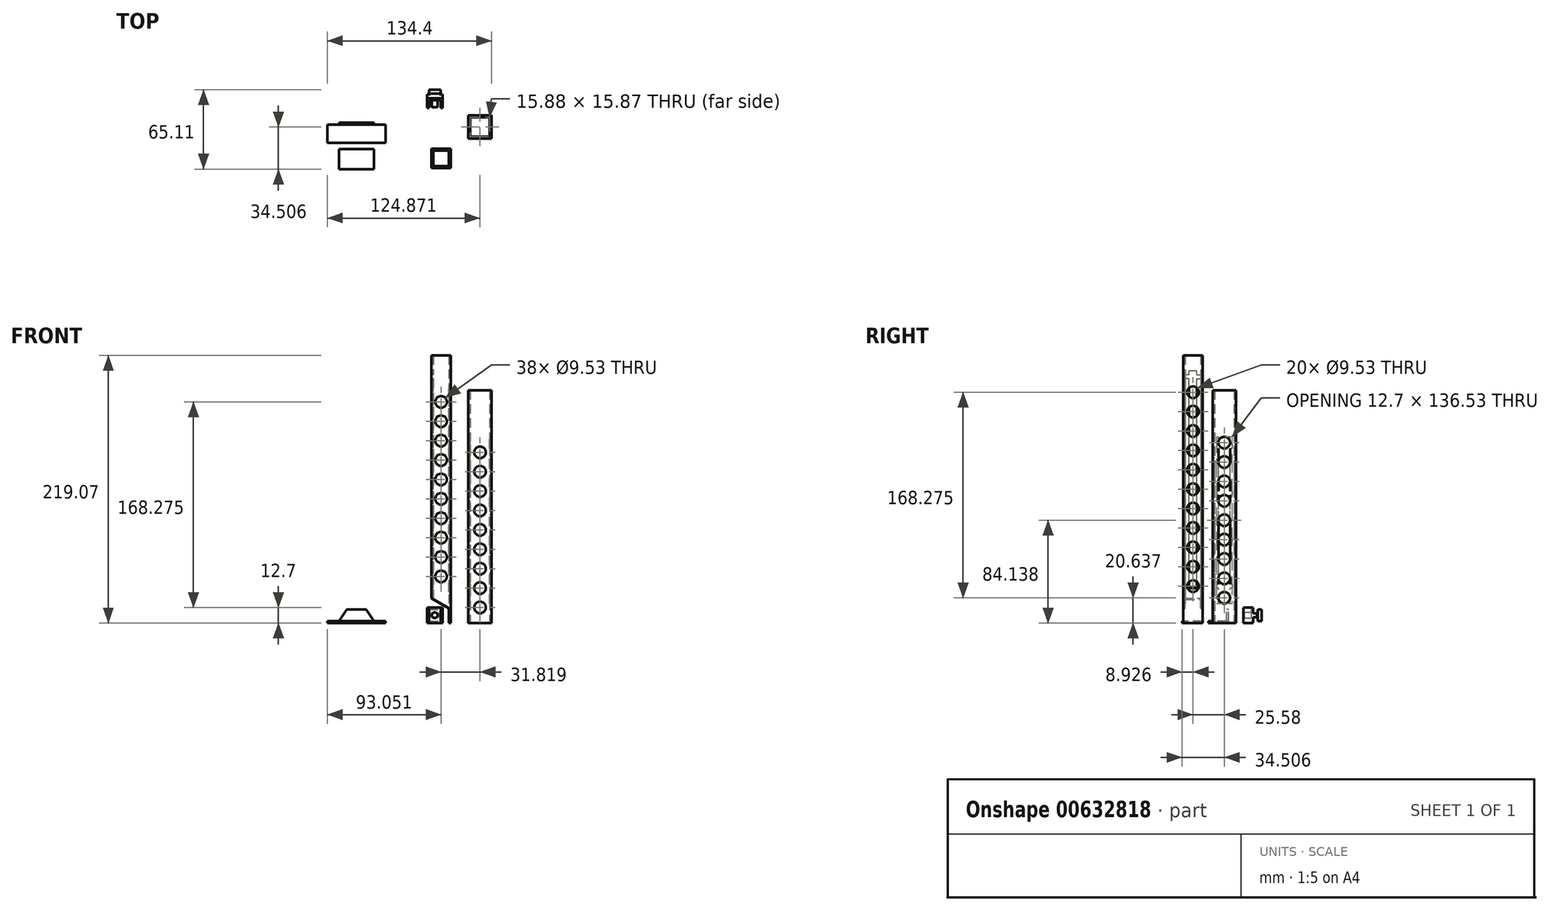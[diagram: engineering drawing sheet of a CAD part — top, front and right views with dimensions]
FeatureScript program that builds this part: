
annotation { "Feature Type Name" : "Feature", "Feature Type Description" : "" }
export const myFeature = defineFeature(function(context is Context, id is Id, definition is map)
    precondition{}
    {
        {
            var Q0;
            Q0=qCreatedBy(makeId("Top.planeOp"),FACE);
            var sketch = newSketch(context, id + "F0", { "sketchPlane" : qUnion([Q0])});
            skLineSegment(sketch, "E0.bottom", {"start": v(48.39, -26.4) * mm, "end": v(67.44, -26.4) * mm});
            skLineSegment(sketch, "E0.top", {"start": v(48.39, -45.46) * mm, "end": v(67.44, -45.46) * mm});
            skLineSegment(sketch, "E0.left", {"start": v(48.39, -26.4) * mm, "end": v(48.39, -45.46) * mm});
            skLineSegment(sketch, "E0.right", {"start": v(67.44, -26.4) * mm, "end": v(67.44, -45.46) * mm});
            skLineSegment(sketch, "E1.0", {"start": v(49.97, -28) * mm, "end": v(49.97, -43.87) * mm});
            skLineSegment(sketch, "E1.1", {"start": v(49.97, -28) * mm, "end": v(65.85, -28) * mm});
            skLineSegment(sketch, "E1.2", {"start": v(65.85, -28) * mm, "end": v(65.85, -43.87) * mm});
            skLineSegment(sketch, "E1.3", {"start": v(49.97, -43.87) * mm, "end": v(65.85, -43.87) * mm});
            skSolve(sketch);
        }
        {
            var Q0;
            Q0=makeQuery(id+"F0.imprint","IMPRINT",FACE,{"disambiguationData":[TD([[makeQuery(id+"F0.imprint","IMPRINT",EDGE,{"derivedFrom":sQuery(id+"F0.wireOp",EDGE,"E0.bottom")}),-1.0]])]});
            extrude(context, id + "F1", {"entities" : qUnion([Q0]), "depth" : 190.5 * mm, "offsetDistance" : 25.4 * mm});
        }
        {
            var Q0;
            Q0=makeQuery(id+"F1.opExtrude","SWEPT_FACE",FACE,{"disambiguationData":[OSD([sQuery(id+"F0.wireOp",EDGE,"E0.top")])]});
            var sketch = newSketch(context, id + "F2", { "sketchPlane" : qUnion([Q0])});
            skLineSegment(sketch, "E2", {"start": v(57.91, 190.5) * mm, "end": v(57.91, 0) * mm, "construction": true});
            skLineSegment(sketch, "E3", {"start": v(67.44, 139.7) * mm, "end": v(48.39, 139.7) * mm, "construction": true});
            skCircle(sketch, "E4", {"center": v(57.91, 139.7) * mm, "radius": 4.76 * mm});
            skCircle(sketch, "E5.0.1.0", {"center": v(57.91, 123.83) * mm, "radius": 4.76 * mm});
            skCircle(sketch, "E5.0.2.0", {"center": v(57.91, 107.95) * mm, "radius": 4.76 * mm});
            skCircle(sketch, "E5.0.3.0", {"center": v(57.91, 92.08) * mm, "radius": 4.76 * mm});
            skCircle(sketch, "E5.0.4.0", {"center": v(57.91, 76.2) * mm, "radius": 4.76 * mm});
            skCircle(sketch, "E5.0.5.0", {"center": v(57.91, 60.33) * mm, "radius": 4.76 * mm});
            skCircle(sketch, "E5.0.6.0", {"center": v(57.91, 44.45) * mm, "radius": 4.76 * mm});
            skCircle(sketch, "E5.0.7.0", {"center": v(57.91, 28.58) * mm, "radius": 4.76 * mm});
            skCircle(sketch, "E5.0.8.0", {"center": v(57.91, 12.7) * mm, "radius": 4.76 * mm});
            skLineSegment(sketch, "E5.direction1", {"start": v(-21.64, 139.7) * mm, "end": v(57.91, 139.7) * mm, "construction": true});
            skLineSegment(sketch, "E5.direction2", {"start": v(57.91, 139.7) * mm, "end": v(57.91, 123.83) * mm, "construction": true});
            skSolve(sketch);
        }
        {
            var Q0;
            Q0 = qSketchRegion(id + "F2", true);
            extrude(context, id + "F3", {"entities" : qUnion([Q0]), "operationType" : NewBodyOperationType.REMOVE, "endBound" : BoundingType.THROUGH_ALL, "oppositeDirection" : true, "depth" : 25.4 * mm, "offsetDistance" : 25.4 * mm});
        }
        {
            var Q0;
            Q0=makeQuery(id+"F1.opExtrude","SWEPT_FACE",FACE,{"disambiguationData":[OSD([sQuery(id+"F0.wireOp",EDGE,"E0.right")])]});
            var sketch = newSketch(context, id + "F4", { "sketchPlane" : qUnion([Q0])});
            skLineSegment(sketch, "E6", {"start": v(-35.93, 190.5) * mm, "end": v(-35.93, 0) * mm, "construction": true});
            skLineSegment(sketch, "E7", {"start": v(-26.4, 147.64) * mm, "end": v(-45.46, 147.64) * mm, "construction": true});
            skCircle(sketch, "E8", {"center": v(-35.93, 147.64) * mm, "radius": 4.76 * mm});
            skCircle(sketch, "E9.0.1.0", {"center": v(-35.93, 131.76) * mm, "radius": 4.76 * mm});
            skCircle(sketch, "E9.0.2.0", {"center": v(-35.93, 115.89) * mm, "radius": 4.76 * mm});
            skCircle(sketch, "E9.0.3.0", {"center": v(-35.93, 100.01) * mm, "radius": 4.76 * mm});
            skCircle(sketch, "E9.0.4.0", {"center": v(-35.93, 84.14) * mm, "radius": 4.76 * mm});
            skCircle(sketch, "E9.0.5.0", {"center": v(-35.93, 68.26) * mm, "radius": 4.76 * mm});
            skCircle(sketch, "E9.0.6.0", {"center": v(-35.93, 52.39) * mm, "radius": 4.76 * mm});
            skCircle(sketch, "E9.0.7.0", {"center": v(-35.93, 36.51) * mm, "radius": 4.76 * mm});
            skLineSegment(sketch, "E9.direction1", {"start": v(-35.93, 147.64) * mm, "end": v(11.04, 147.64) * mm, "construction": true});
            skLineSegment(sketch, "E9.direction2", {"start": v(-35.93, 147.64) * mm, "end": v(-35.93, 131.76) * mm, "construction": true});
            skCircle(sketch, "E10.0.0.8", {"center": v(-35.93, 20.64) * mm, "radius": 4.76 * mm});
            skSolve(sketch);
        }
        {
            var Q0;
            Q0 = qSketchRegion(id + "F4", true);
            extrude(context, id + "F5", {"entities" : qUnion([Q0]), "operationType" : NewBodyOperationType.REMOVE, "endBound" : BoundingType.UP_TO_NEXT, "oppositeDirection" : true, "depth" : 25.4 * mm, "offsetDistance" : 25.4 * mm});
        }
        {
            var Q0;
            Q0=makeQuery(id+"F1.opExtrude","SWEPT_FACE",FACE,{"disambiguationData":[OSD([sQuery(id+"F0.wireOp",EDGE,"E0.left")])]});
            var sketch = newSketch(context, id + "F6", { "sketchPlane" : qUnion([Q0])});
            skLineSegment(sketch, "E11", {"start": v(45.46, 15.88) * mm, "end": v(26.4, 15.88) * mm, "construction": true});
            skLineSegment(sketch, "E12", {"start": v(26.4, 152.4) * mm, "end": v(45.46, 152.4) * mm, "construction": true});
            skLineSegment(sketch, "E13", {"start": v(31.17, 0) * mm, "end": v(31.17, 190.5) * mm, "construction": true});
            skLineSegment(sketch, "E14", {"start": v(40.7, 0) * mm, "end": v(40.7, 190.5) * mm, "construction": true});
            skLineSegment(sketch, "E15.bottom", {"start": v(31.17, 15.88) * mm, "end": v(40.7, 15.88) * mm});
            skLineSegment(sketch, "E15.top", {"start": v(31.17, 152.4) * mm, "end": v(40.7, 152.4) * mm});
            skLineSegment(sketch, "E15.left", {"start": v(31.17, 15.88) * mm, "end": v(31.17, 152.4) * mm});
            skLineSegment(sketch, "E15.right", {"start": v(40.7, 15.88) * mm, "end": v(40.7, 152.4) * mm});
            skSolve(sketch);
        }
        {
            var Q0;
            Q0 = qSketchRegion(id + "F6", true);
            extrude(context, id + "F7", {"entities" : qUnion([Q0]), "operationType" : NewBodyOperationType.REMOVE, "endBound" : BoundingType.UP_TO_NEXT, "oppositeDirection" : true, "depth" : 25.4 * mm, "offsetDistance" : 25.4 * mm});
        }
        {
            var Q0;
            Q0=makeQuery(id+"F1.opExtrude","SWEPT_FACE",FACE,{"disambiguationData":[OSD([sQuery(id+"F0.wireOp",EDGE,"E0.left")])]});
            var sketch = newSketch(context, id + "F8", { "sketchPlane" : qUnion([Q0])});
            skLineSegment(sketch, "E16.bottom", {"start": v(29.58, 146.05) * mm, "end": v(31.17, 146.05) * mm});
            skLineSegment(sketch, "E16.top", {"start": v(29.58, 142.88) * mm, "end": v(31.17, 142.88) * mm});
            skLineSegment(sketch, "E16.left", {"start": v(29.58, 146.05) * mm, "end": v(29.58, 142.88) * mm});
            skLineSegment(sketch, "E16.right", {"start": v(31.17, 146.05) * mm, "end": v(31.17, 142.88) * mm});
            skLineSegment(sketch, "E17.0.1.0", {"start": v(29.58, 107.95) * mm, "end": v(31.17, 107.95) * mm});
            skLineSegment(sketch, "E17.0.1.1", {"start": v(29.58, 107.95) * mm, "end": v(29.58, 104.78) * mm});
            skLineSegment(sketch, "E17.0.1.2", {"start": v(29.58, 104.78) * mm, "end": v(31.17, 104.78) * mm});
            skLineSegment(sketch, "E17.0.1.3", {"start": v(31.17, 107.95) * mm, "end": v(31.17, 104.78) * mm});
            skLineSegment(sketch, "E17.0.2.0", {"start": v(29.58, 69.85) * mm, "end": v(31.17, 69.85) * mm});
            skLineSegment(sketch, "E17.0.2.1", {"start": v(29.58, 69.85) * mm, "end": v(29.58, 66.68) * mm});
            skLineSegment(sketch, "E17.0.2.2", {"start": v(29.58, 66.68) * mm, "end": v(31.17, 66.68) * mm});
            skLineSegment(sketch, "E17.0.2.3", {"start": v(31.17, 69.85) * mm, "end": v(31.17, 66.68) * mm});
            skLineSegment(sketch, "E17.0.3.0", {"start": v(29.58, 31.75) * mm, "end": v(31.17, 31.75) * mm});
            skLineSegment(sketch, "E17.0.3.1", {"start": v(29.58, 31.75) * mm, "end": v(29.58, 28.58) * mm});
            skLineSegment(sketch, "E17.0.3.2", {"start": v(29.58, 28.58) * mm, "end": v(31.17, 28.58) * mm});
            skLineSegment(sketch, "E17.0.3.3", {"start": v(31.17, 31.75) * mm, "end": v(31.17, 28.58) * mm});
            skLineSegment(sketch, "E17.1.0.0", {"start": v(40.7, 146.05) * mm, "end": v(42.28, 146.05) * mm});
            skLineSegment(sketch, "E17.1.0.1", {"start": v(40.7, 146.05) * mm, "end": v(40.7, 142.88) * mm});
            skLineSegment(sketch, "E17.1.0.2", {"start": v(40.7, 142.88) * mm, "end": v(42.28, 142.88) * mm});
            skLineSegment(sketch, "E17.1.0.3", {"start": v(42.28, 146.05) * mm, "end": v(42.28, 142.88) * mm});
            skLineSegment(sketch, "E17.1.1.0", {"start": v(40.7, 107.95) * mm, "end": v(42.28, 107.95) * mm});
            skLineSegment(sketch, "E17.1.1.1", {"start": v(40.7, 107.95) * mm, "end": v(40.7, 104.78) * mm});
            skLineSegment(sketch, "E17.1.1.2", {"start": v(40.7, 104.78) * mm, "end": v(42.28, 104.78) * mm});
            skLineSegment(sketch, "E17.1.1.3", {"start": v(42.28, 107.95) * mm, "end": v(42.28, 104.78) * mm});
            skLineSegment(sketch, "E17.1.2.0", {"start": v(40.7, 69.85) * mm, "end": v(42.28, 69.85) * mm});
            skLineSegment(sketch, "E17.1.2.1", {"start": v(40.7, 69.85) * mm, "end": v(40.7, 66.68) * mm});
            skLineSegment(sketch, "E17.1.2.2", {"start": v(40.7, 66.68) * mm, "end": v(42.28, 66.68) * mm});
            skLineSegment(sketch, "E17.1.2.3", {"start": v(42.28, 69.85) * mm, "end": v(42.28, 66.68) * mm});
            skLineSegment(sketch, "E17.1.3.0", {"start": v(40.7, 31.75) * mm, "end": v(42.28, 31.75) * mm});
            skLineSegment(sketch, "E17.1.3.1", {"start": v(40.7, 31.75) * mm, "end": v(40.7, 28.58) * mm});
            skLineSegment(sketch, "E17.1.3.2", {"start": v(40.7, 28.58) * mm, "end": v(42.28, 28.58) * mm});
            skLineSegment(sketch, "E17.1.3.3", {"start": v(42.28, 31.75) * mm, "end": v(42.28, 28.58) * mm});
            skLineSegment(sketch, "E17.direction1", {"start": v(29.58, 146.05) * mm, "end": v(40.7, 146.05) * mm, "construction": true});
            skLineSegment(sketch, "E17.direction2", {"start": v(29.58, 146.05) * mm, "end": v(29.58, 107.95) * mm, "construction": true});
            skSolve(sketch);
        }
        {
            var Q0;
            Q0 = qSketchRegion(id + "F8", true);
            extrude(context, id + "F9", {"entities" : qUnion([Q0]), "operationType" : NewBodyOperationType.REMOVE, "endBound" : BoundingType.UP_TO_NEXT, "oppositeDirection" : true, "depth" : 25.4 * mm, "offsetDistance" : 25.4 * mm});
        }
        {
            var Q0;
            Q0=qCreatedBy(makeId("Top.planeOp"),FACE);
            var sketch = newSketch(context, id + "F10", { "sketchPlane" : qUnion([Q0])});
            skLineSegment(sketch, "E18.bottom", {"start": v(18.15, -53.58) * mm, "end": v(34.03, -53.58) * mm});
            skLineSegment(sketch, "E18.top", {"start": v(18.15, -69.45) * mm, "end": v(34.03, -69.45) * mm});
            skLineSegment(sketch, "E18.left", {"start": v(18.15, -53.58) * mm, "end": v(18.15, -69.45) * mm});
            skLineSegment(sketch, "E18.right", {"start": v(34.03, -53.58) * mm, "end": v(34.03, -69.45) * mm});
            skLineSegment(sketch, "E19.0", {"start": v(32.44, -55.16) * mm, "end": v(32.44, -67.86) * mm});
            skLineSegment(sketch, "E19.1", {"start": v(19.74, -55.16) * mm, "end": v(32.44, -55.16) * mm});
            skLineSegment(sketch, "E19.2", {"start": v(19.74, -55.16) * mm, "end": v(19.74, -67.86) * mm});
            skLineSegment(sketch, "E19.3", {"start": v(19.74, -67.86) * mm, "end": v(32.44, -67.86) * mm});
            skSolve(sketch);
        }
        {
            var Q0;
            Q0 = qSketchRegion(id + "F10", true);
            extrude(context, id + "F11", {"entities" : qUnion([Q0]), "depth" : 219.07 * mm, "offsetDistance" : 25.4 * mm});
        }
        {
            var Q0;
            Q0=makeQuery(id+"F11.opExtrude","SWEPT_FACE",FACE,{"disambiguationData":[OSD([sQuery(id+"F10.wireOp",EDGE,"E18.top")])]});
            var sketch = newSketch(context, id + "F12", { "sketchPlane" : qUnion([Q0])});
            skLineSegment(sketch, "E20", {"start": v(26.1, 219.08) * mm, "end": v(26.1, 0) * mm, "construction": true});
            skLineSegment(sketch, "E21", {"start": v(18.15, 38.1) * mm, "end": v(34.03, 38.1) * mm, "construction": true});
            skCircle(sketch, "E22", {"center": v(26.1, 38.1) * mm, "radius": 4.76 * mm});
            skCircle(sketch, "E23.0.1.0", {"center": v(26.1, 53.97) * mm, "radius": 4.76 * mm});
            skCircle(sketch, "E23.0.2.0", {"center": v(26.1, 69.85) * mm, "radius": 4.76 * mm});
            skCircle(sketch, "E23.0.3.0", {"center": v(26.1, 85.72) * mm, "radius": 4.76 * mm});
            skCircle(sketch, "E23.0.4.0", {"center": v(26.1, 101.6) * mm, "radius": 4.76 * mm});
            skCircle(sketch, "E23.0.5.0", {"center": v(26.1, 117.47) * mm, "radius": 4.76 * mm});
            skCircle(sketch, "E23.0.6.0", {"center": v(26.1, 133.35) * mm, "radius": 4.76 * mm});
            skCircle(sketch, "E23.0.7.0", {"center": v(26.1, 149.22) * mm, "radius": 4.76 * mm});
            skCircle(sketch, "E23.0.8.0", {"center": v(26.1, 165.1) * mm, "radius": 4.76 * mm});
            skLineSegment(sketch, "E23.direction1", {"start": v(26.1, 38.1) * mm, "end": v(55.72, 38.1) * mm, "construction": true});
            skLineSegment(sketch, "E23.direction2", {"start": v(26.1, 38.1) * mm, "end": v(26.1, 53.97) * mm, "construction": true});
            skCircle(sketch, "E24.0.0.9", {"center": v(26.1, 180.97) * mm, "radius": 4.76 * mm});
            skSolve(sketch);
        }
        {
            var Q0;
            Q0 = qSketchRegion(id + "F12", true);
            extrude(context, id + "F13", {"entities" : qUnion([Q0]), "operationType" : NewBodyOperationType.REMOVE, "endBound" : BoundingType.THROUGH_ALL, "oppositeDirection" : true, "depth" : 25.4 * mm, "offsetDistance" : 25.4 * mm});
        }
        {
            var Q0;
            Q0=makeQuery(id+"F11.opExtrude","SWEPT_FACE",FACE,{"disambiguationData":[OSD([sQuery(id+"F10.wireOp",EDGE,"E18.right")])]});
            var sketch = newSketch(context, id + "F14", { "sketchPlane" : qUnion([Q0])});
            skLineSegment(sketch, "E25", {"start": v(-61.51, 219.08) * mm, "end": v(-61.51, 0) * mm, "construction": true});
            skLineSegment(sketch, "E26", {"start": v(-69.45, 30.16) * mm, "end": v(-53.58, 30.16) * mm, "construction": true});
            skCircle(sketch, "E27", {"center": v(-61.51, 30.16) * mm, "radius": 4.76 * mm});
            skCircle(sketch, "E28.0.1.0", {"center": v(-61.51, 46.04) * mm, "radius": 4.76 * mm});
            skCircle(sketch, "E28.0.2.0", {"center": v(-61.51, 61.91) * mm, "radius": 4.76 * mm});
            skCircle(sketch, "E28.0.3.0", {"center": v(-61.51, 77.79) * mm, "radius": 4.76 * mm});
            skCircle(sketch, "E28.0.4.0", {"center": v(-61.51, 93.66) * mm, "radius": 4.76 * mm});
            skCircle(sketch, "E28.0.5.0", {"center": v(-61.51, 109.54) * mm, "radius": 4.76 * mm});
            skCircle(sketch, "E28.0.6.0", {"center": v(-61.51, 125.41) * mm, "radius": 4.76 * mm});
            skCircle(sketch, "E28.0.7.0", {"center": v(-61.51, 141.29) * mm, "radius": 4.76 * mm});
            skLineSegment(sketch, "E28.direction1", {"start": v(-61.51, 30.16) * mm, "end": v(-36.11, 30.16) * mm, "construction": true});
            skLineSegment(sketch, "E28.direction2", {"start": v(-61.51, 30.16) * mm, "end": v(-61.51, 46.04) * mm, "construction": true});
            skCircle(sketch, "E29.0.0.8", {"center": v(-61.51, 157.16) * mm, "radius": 4.76 * mm});
            skCircle(sketch, "E29.0.0.9", {"center": v(-61.51, 173.04) * mm, "radius": 4.76 * mm});
            skCircle(sketch, "E30.0.0.10", {"center": v(-61.51, 188.91) * mm, "radius": 4.76 * mm});
            skSolve(sketch);
        }
        {
            var Q0;
            Q0 = qSketchRegion(id + "F14", true);
            extrude(context, id + "F15", {"entities" : qUnion([Q0]), "operationType" : NewBodyOperationType.REMOVE, "endBound" : BoundingType.UP_TO_NEXT, "oppositeDirection" : true, "depth" : 25.4 * mm, "offsetDistance" : 25.4 * mm});
        }
        {
            var Q0;
            Q0=makeQuery(id+"F11.opExtrude","SWEPT_FACE",FACE,{"disambiguationData":[OSD([sQuery(id+"F10.wireOp",EDGE,"E18.left")])]});
            var sketch = newSketch(context, id + "F16", { "sketchPlane" : qUnion([Q0])});
            skLineSegment(sketch, "E31", {"start": v(53.58, 206.38) * mm, "end": v(69.45, 206.38) * mm, "construction": true});
            skLineSegment(sketch, "E32", {"start": v(69.45, 28.58) * mm, "end": v(53.58, 28.58) * mm, "construction": true});
            skLineSegment(sketch, "E33", {"start": v(58.34, 28.58) * mm, "end": v(58.34, 206.38) * mm, "construction": true});
            skLineSegment(sketch, "E34", {"start": v(64.69, 206.38) * mm, "end": v(64.69, 28.58) * mm, "construction": true});
            skLineSegment(sketch, "E35.bottom", {"start": v(58.34, 28.58) * mm, "end": v(64.69, 28.58) * mm});
            skLineSegment(sketch, "E35.top", {"start": v(58.34, 206.38) * mm, "end": v(64.69, 206.38) * mm});
            skLineSegment(sketch, "E35.left", {"start": v(58.34, 28.58) * mm, "end": v(58.34, 206.38) * mm});
            skLineSegment(sketch, "E35.right", {"start": v(64.69, 28.58) * mm, "end": v(64.69, 206.38) * mm});
            skSolve(sketch);
        }
        {
            var Q0;
            Q0 = qSketchRegion(id + "F16", true);
            extrude(context, id + "F17", {"entities" : qUnion([Q0]), "operationType" : NewBodyOperationType.REMOVE, "endBound" : BoundingType.UP_TO_NEXT, "oppositeDirection" : true, "depth" : 25.4 * mm, "offsetDistance" : 25.4 * mm});
        }
        {
            var Q0;
            Q0=makeQuery(id+"F11.opExtrude","SWEPT_FACE",FACE,{"disambiguationData":[OSD([sQuery(id+"F10.wireOp",EDGE,"E18.bottom")])]});
            var sketch = newSketch(context, id + "F18", { "sketchPlane" : qUnion([Q0])});
            skLineSegment(sketch, "E36", {"start": v(-32.44, 11.9) * mm, "end": v(-18.15, 20.16) * mm});
            skLineSegment(sketch, "E37", {"start": v(-32.44, 0) * mm, "end": v(-32.44, 11.9) * mm});
            skSolve(sketch);
        }
        {
            var Q0;
            {var subQ0=sQuery(id+"F18.wireOp",EDGE,"E36");Q0=makeQuery(id+"F18.imprint","IMPRINT",FACE,{"disambiguationData":[TD([[makeQuery(id+"F18.imprint","IMPRINT",EDGE,{"derivedFrom":subQ0}),-1.0]])]});}
            extrude(context, id + "F19", {"entities" : qUnion([Q0]), "operationType" : NewBodyOperationType.REMOVE, "oppositeDirection" : true, "depth" : 15.88 * mm, "offsetDistance" : 25.4 * mm});
        }
        {
            var Q0;
            Q0=makeQuery(id+"F11.opExtrude","SWEPT_FACE",FACE,{"disambiguationData":[OSD([sQuery(id+"F10.wireOp",EDGE,"E18.left")])]});
            var sketch = newSketch(context, id + "F20", { "sketchPlane" : qUnion([Q0])});
            skLineSegment(sketch, "E38.bottom", {"start": v(58.34, 203.2) * mm, "end": v(55.16, 203.2) * mm});
            skLineSegment(sketch, "E38.top", {"start": v(58.34, 200.03) * mm, "end": v(55.16, 200.03) * mm});
            skLineSegment(sketch, "E38.left", {"start": v(58.34, 203.2) * mm, "end": v(58.34, 200.03) * mm});
            skLineSegment(sketch, "E38.right", {"start": v(55.16, 203.2) * mm, "end": v(55.16, 200.03) * mm});
            skLineSegment(sketch, "E39", {"start": v(61.51, 219.08) * mm, "end": v(61.51, 182.16) * mm, "construction": true});
            skLineSegment(sketch, "E40.MirrorCS", {"start": v(64.69, 200.03) * mm, "end": v(67.86, 200.03) * mm});
            skLineSegment(sketch, "E41.MirrorCS", {"start": v(64.69, 203.2) * mm, "end": v(64.69, 200.03) * mm});
            skLineSegment(sketch, "E42.MirrorCS", {"start": v(67.86, 203.2) * mm, "end": v(67.86, 200.03) * mm});
            skLineSegment(sketch, "E43.MirrorCS", {"start": v(64.69, 203.2) * mm, "end": v(67.86, 203.2) * mm});
            skSolve(sketch);
        }
        {
            var Q0;
            Q0 = qSketchRegion(id + "F20", true);
            extrude(context, id + "F21", {"entities" : qUnion([Q0]), "operationType" : NewBodyOperationType.REMOVE, "endBound" : BoundingType.UP_TO_NEXT, "oppositeDirection" : true, "depth" : 25.4 * mm, "offsetDistance" : 25.4 * mm});
        }
        {
            var Q0;
            Q0=qCreatedBy(makeId("Top.planeOp"),FACE);
            var sketch = newSketch(context, id + "F22", { "sketchPlane" : qUnion([Q0])});
            skLineSegment(sketch, "E44.bottom", {"start": v(14.55, -12.47) * mm, "end": v(27.25, -12.47) * mm});
            skLineSegment(sketch, "E44.top", {"start": v(14.55, -20.4) * mm, "end": v(16.14, -20.4) * mm});
            skLineSegment(sketch, "E44.left", {"start": v(14.55, -12.47) * mm, "end": v(14.55, -20.4) * mm});
            skLineSegment(sketch, "E44.right", {"start": v(27.25, -12.47) * mm, "end": v(27.25, -20.4) * mm});
            skLineSegment(sketch, "E45.top", {"start": v(16.14, -14.06) * mm, "end": v(25.66, -14.06) * mm});
            skLineSegment(sketch, "E45.left", {"start": v(16.14, -20.4) * mm, "end": v(16.14, -14.06) * mm});
            skLineSegment(sketch, "E45.right", {"start": v(25.66, -20.4) * mm, "end": v(25.66, -14.06) * mm});
            skLineSegment(sketch, "E46.trimOffspring", {"start": v(25.66, -20.4) * mm, "end": v(27.25, -20.4) * mm});
            skSolve(sketch);
        }
        {
            var Q0;
            Q0 = qSketchRegion(id + "F22", true);
            extrude(context, id + "F23", {"entities" : qUnion([Q0]), "depth" : 12.7 * mm, "offsetDistance" : 25.4 * mm});
        }
        {
            var Q0;
            Q0=makeQuery(id+"F23.opExtrude","SWEPT_FACE",FACE,{"disambiguationData":[OSD([sQuery(id+"F22.wireOp",EDGE,"E45.top")])]});
            var sketch = newSketch(context, id + "F24", { "sketchPlane" : qUnion([Q0])});
            skLineSegment(sketch, "E47", {"start": v(25.66, 12.7) * mm, "end": v(16.14, 0) * mm, "construction": true});
            skLineSegment(sketch, "E48", {"start": v(25.66, 0) * mm, "end": v(16.14, 12.7) * mm, "construction": true});
            skCircle(sketch, "E49", {"center": v(20.9, 6.35) * mm, "radius": 2.38 * mm});
            skSolve(sketch);
        }
        {
            var Q0;
            Q0 = qSketchRegion(id + "F24", true);
            extrude(context, id + "F25", {"entities" : qUnion([Q0]), "operationType" : NewBodyOperationType.ADD, "depth" : 5.56 * mm, "offsetDistance" : 25.4 * mm});
        }
        {
            var Q0;
            Q0=makeQuery(id+"F23.opExtrude","SWEPT_FACE",FACE,{"disambiguationData":[OSD([sQuery(id+"F22.wireOp",EDGE,"E44.bottom")])]});
            var sketch = newSketch(context, id + "F26", { "sketchPlane" : qUnion([Q0])});
            skLineSegment(sketch, "E50.bottom", {"start": v(-27.25, 7.94) * mm, "end": v(-14.55, 7.94) * mm});
            skLineSegment(sketch, "E50.top", {"start": v(-27.25, 4.76) * mm, "end": v(-14.55, 4.76) * mm});
            skLineSegment(sketch, "E50.left", {"start": v(-27.25, 7.94) * mm, "end": v(-27.25, 4.76) * mm});
            skLineSegment(sketch, "E50.right", {"start": v(-14.55, 7.94) * mm, "end": v(-14.55, 4.76) * mm});
            skSolve(sketch);
        }
        {
            var Q0;
            Q0=makeQuery(id+"F26.imprint","IMPRINT",FACE,{"disambiguationData":[TD([[makeQuery(id+"F26.imprint","IMPRINT",EDGE,{"derivedFrom":sQuery(id+"F26.wireOp",EDGE,"E50.bottom")}),-1.0]])]});
            extrude(context, id + "F27", {"entities" : qUnion([Q0]), "operationType" : NewBodyOperationType.ADD, "depth" : 3.17 * mm, "offsetDistance" : 25.4 * mm});
        }
        {
            var Q0;
            Q0=makeQuery(id+"F27.opExtrude","CAP_FACE",FACE,{"disambiguationData":[OSD([sQuery(id+"F26.wireOp",EDGE,"E50.bottom"),sQuery(id+"F26.wireOp",EDGE,"E50.top"),sQuery(id+"F26.wireOp",EDGE,"E50.left"),sQuery(id+"F26.wireOp",EDGE,"E50.right")])],"isStart":false});
            var sketch = newSketch(context, id + "F28", { "sketchPlane" : qUnion([Q0])});
            skLineSegment(sketch, "E51.bottom", {"start": v(-24.71, 7.94) * mm, "end": v(-17.1, 7.94) * mm});
            skLineSegment(sketch, "E51.top", {"start": v(-24.71, 4.76) * mm, "end": v(-17.1, 4.76) * mm});
            skLineSegment(sketch, "E51.left", {"start": v(-24.71, 7.94) * mm, "end": v(-24.71, 4.76) * mm});
            skLineSegment(sketch, "E51.right", {"start": v(-17.1, 7.94) * mm, "end": v(-17.1, 4.76) * mm});
            skSolve(sketch);
        }
        {
            var Q0;
            Q0 = qSketchRegion(id + "F28", true);
            extrude(context, id + "F29", {"entities" : qUnion([Q0]), "operationType" : NewBodyOperationType.ADD, "depth" : 0.8 * mm, "offsetDistance" : 25.4 * mm});
        }
        {
            var Q0;
            Q0=makeQuery(id+"F29.opExtrude","CAP_FACE",FACE,{"disambiguationData":[OSD([sQuery(id+"F28.wireOp",EDGE,"E51.bottom"),sQuery(id+"F28.wireOp",EDGE,"E51.top"),sQuery(id+"F28.wireOp",EDGE,"E51.left"),sQuery(id+"F28.wireOp",EDGE,"E51.right")])],"isStart":false});
            cPlane(context, id + "F30", {"entities" : qUnion([Q0]), "cplaneType" : CPlaneType.OFFSET, "offset" : 0 * mm, "width" : 152.4 * mm, "height" : 152.4 * mm});
        }
        {
            var Q0;
            Q0=qCreatedBy(id+"F30.planeOp",FACE);
            var sketch = newSketch(context, id + "F31", { "sketchPlane" : qUnion([Q0])});
            skLineSegment(sketch, "E52.bottom", {"start": v(-16.14, 1.59) * mm, "end": v(-25.66, 1.59) * mm});
            skLineSegment(sketch, "E52.top", {"start": v(-16.14, 11.11) * mm, "end": v(-25.66, 11.11) * mm});
            skLineSegment(sketch, "E52.left", {"start": v(-16.14, 1.59) * mm, "end": v(-16.14, 11.11) * mm});
            skLineSegment(sketch, "E52.right", {"start": v(-25.66, 1.59) * mm, "end": v(-25.66, 11.11) * mm});
            skSolve(sketch);
        }
        {
            var Q0;
            Q0 = qSketchRegion(id + "F31", true);
            extrude(context, id + "F32", {"entities" : qUnion([Q0]), "operationType" : NewBodyOperationType.ADD, "depth" : 3.17 * mm, "offsetDistance" : 25.4 * mm});
        }
        {
            var Q0;
            Q0=qCreatedBy(makeId("Top.planeOp"),FACE);
            var sketch = newSketch(context, id + "F33", { "sketchPlane" : qUnion([Q0])});
            skLineSegment(sketch, "E53.bottom", {"start": v(-57.32, -53.93) * mm, "end": v(-28.75, -53.93) * mm});
            skLineSegment(sketch, "E53.top", {"start": v(-57.32, -70.44) * mm, "end": v(-28.75, -70.44) * mm});
            skLineSegment(sketch, "E53.left", {"start": v(-57.32, -53.93) * mm, "end": v(-57.32, -70.44) * mm});
            skLineSegment(sketch, "E53.right", {"start": v(-28.75, -53.93) * mm, "end": v(-28.75, -70.44) * mm});
            skSolve(sketch);
        }
        {
            var Q0;
            Q0 = qSketchRegion(id + "F33", true);
            extrude(context, id + "F34", {"entities" : qUnion([Q0]), "depth" : 1.59 * mm, "offsetDistance" : 25.4 * mm});
        }
        {
            var Q0;
            Q0=qCreatedBy(makeId("Top.planeOp"),FACE);
            var sketch = newSketch(context, id + "F35", { "sketchPlane" : qUnion([Q0])});
            skLineSegment(sketch, "E54.right", {"start": v(-66.96, -34.02) * mm, "end": v(-66.96, -49) * mm});
            skLineSegment(sketch, "E55.right", {"start": v(-19.33, -34.02) * mm, "end": v(-19.33, -49) * mm});
            skLineSegment(sketch, "E56", {"start": v(-66.96, -49) * mm, "end": v(-19.33, -49) * mm});
            skLineSegment(sketch, "E57", {"start": v(-66.96, -34.02) * mm, "end": v(-19.33, -34.02) * mm});
            skLineSegment(sketch, "E58.bottom", {"start": v(-57.43, -34.02) * mm, "end": v(-28.86, -34.02) * mm});
            skLineSegment(sketch, "E58.top", {"start": v(-57.43, -32.43) * mm, "end": v(-28.86, -32.43) * mm});
            skLineSegment(sketch, "E58.left", {"start": v(-57.43, -34.02) * mm, "end": v(-57.43, -32.43) * mm});
            skLineSegment(sketch, "E58.right", {"start": v(-28.86, -34.02) * mm, "end": v(-28.86, -32.43) * mm});
            skSolve(sketch);
        }
        {
            var Q0;
            Q0 = qSketchRegion(id + "F35", true);
            extrude(context, id + "F36", {"entities" : qUnion([Q0]), "depth" : 1.59 * mm, "offsetDistance" : 25.4 * mm});
        }
        {
            var Q0;
            Q0=makeQuery(id+"F36.opExtrude","CAP_FACE",FACE,{"disambiguationData":[OSD([sQuery(id+"F35.wireOp",EDGE,"E54.right"),sQuery(id+"F35.wireOp",EDGE,"E55.right"),sQuery(id+"F35.wireOp",EDGE,"E56"),sQuery(id+"F35.wireOp",EDGE,"E57"),sQuery(id+"F35.wireOp",EDGE,"E58.top"),sQuery(id+"F35.wireOp",EDGE,"E58.left"),sQuery(id+"F35.wireOp",EDGE,"E58.right")])],"isStart":false});
            var sketch = newSketch(context, id + "F37", { "sketchPlane" : qUnion([Q0])});
            skLineSegment(sketch, "E59.bottom", {"start": v(-57.43, -32.43) * mm, "end": v(-28.86, -32.43) * mm});
            skLineSegment(sketch, "E59.top", {"start": v(-57.43, -34.02) * mm, "end": v(-28.86, -34.02) * mm});
            skLineSegment(sketch, "E59.left", {"start": v(-57.43, -32.43) * mm, "end": v(-57.43, -34.02) * mm});
            skLineSegment(sketch, "E59.right", {"start": v(-28.86, -32.43) * mm, "end": v(-28.86, -34.02) * mm});
            skSolve(sketch);
        }
        {
            var Q0;
            Q0 = qSketchRegion(id + "F37", true);
            extrude(context, id + "F38", {"entities" : qUnion([Q0]), "operationType" : NewBodyOperationType.ADD, "depth" : 9.52 * mm, "offsetDistance" : 25.4 * mm});
        }
        {
            var Q0;
            Q0=makeQuery(id+"F38.opExtrude","SWEPT_FACE",FACE,{"disambiguationData":[OSD([sQuery(id+"F37.wireOp",EDGE,"E59.top")])]});
            var sketch = newSketch(context, id + "F39", { "sketchPlane" : qUnion([Q0])});
            skLineSegment(sketch, "E60", {"start": v(-57.43, 1.59) * mm, "end": v(-51.08, 11.11) * mm});
            skLineSegment(sketch, "E61", {"start": v(-28.86, 1.59) * mm, "end": v(-35.2, 11.11) * mm});
            skSolve(sketch);
        }
        {
            var Q0;
            {var subQ0=sQuery(id+"F39.wireOp",EDGE,"E60");Q0=makeQuery(id+"F39.imprint","IMPRINT",FACE,{"disambiguationData":[TD([[makeQuery(id+"F39.imprint","IMPRINT",EDGE,{"derivedFrom":subQ0}),1.0]])]});}
            var Q1;
            {var subQ0=sQuery(id+"F39.wireOp",EDGE,"E61");Q1=makeQuery(id+"F39.imprint","IMPRINT",FACE,{"disambiguationData":[TD([[makeQuery(id+"F39.imprint","IMPRINT",EDGE,{"derivedFrom":subQ0}),-1.0]])]});}
            extrude(context, id + "F40", {"entities" : qUnion([Q0, Q1]), "operationType" : NewBodyOperationType.REMOVE, "endBound" : BoundingType.UP_TO_NEXT, "oppositeDirection" : true, "depth" : 25.4 * mm, "offsetDistance" : 25.4 * mm});
        }
    });
